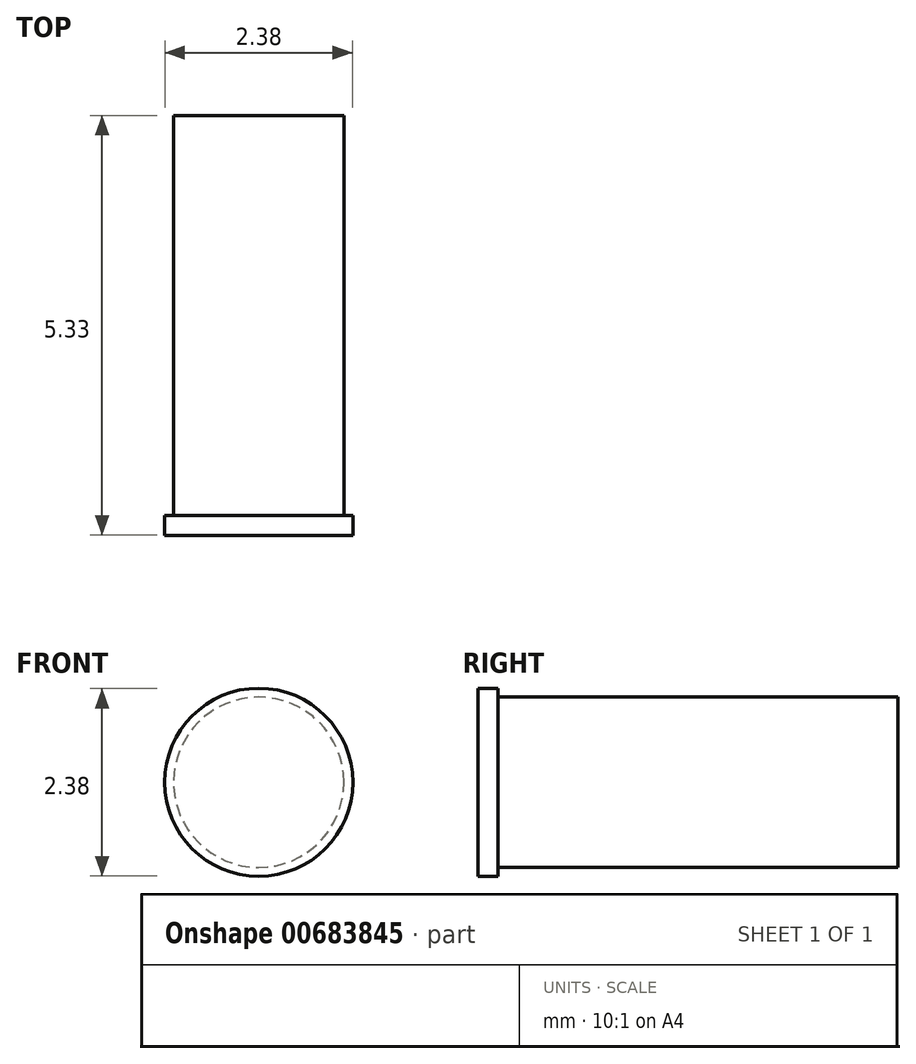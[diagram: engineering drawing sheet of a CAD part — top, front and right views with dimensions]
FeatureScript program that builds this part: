
annotation { "Feature Type Name" : "Feature", "Feature Type Description" : "" }
export const myFeature = defineFeature(function(context is Context, id is Id, definition is map)
    precondition{}
    {
        {
            var Q0;
            Q0=qCreatedBy(makeId("Front.planeOp"),FACE);
            var sketch = newSketch(context, id + "F0", { "sketchPlane" : qUnion([Q0])});
            skCircle(sketch, "E0", {"center": v(0, 0) * mm, "radius": 1.08 * mm});
            skSolve(sketch);
        }
        {
            var Q0;
            Q0=makeQuery(id+"F0.imprint","IMPRINT",FACE,{"disambiguationData":[TD([[makeQuery(id+"F0.imprint","IMPRINT",EDGE,{"derivedFrom":sQuery(id+"F0.wireOp",EDGE,"E0")}),1.0]])]});
            extrude(context, id + "F1", {"entities" : qUnion([Q0]), "depth" : 2.54 * mm, "offsetDistance" : 25.4 * mm, "hasSecondDirection" : true, "secondDirectionOppositeDirection" : true, "secondDirectionDepth" : 2.54 * mm});
        }
        {
            var Q0;
            Q0=makeQuery(id+"F1.opExtrude","CAP_FACE",FACE,{"disambiguationData":[OSD([sQuery(id+"F0.wireOp",EDGE,"E0")])],"isStart":false});
            var sketch = newSketch(context, id + "F2", { "sketchPlane" : qUnion([Q0])});
            skCircle(sketch, "E1", {"center": v(0, 0) * mm, "radius": 1.2 * mm});
            skSolve(sketch);
        }
        {
            var Q0;
            Q0=qSketchRegion(id+"F2",true);
            extrude(context, id + "F3", {"entities" : qUnion([Q0]), "operationType" : NewBodyOperationType.ADD, "depth" : 0.25 * mm, "offsetDistance" : 25.4 * mm});
        }
    });
